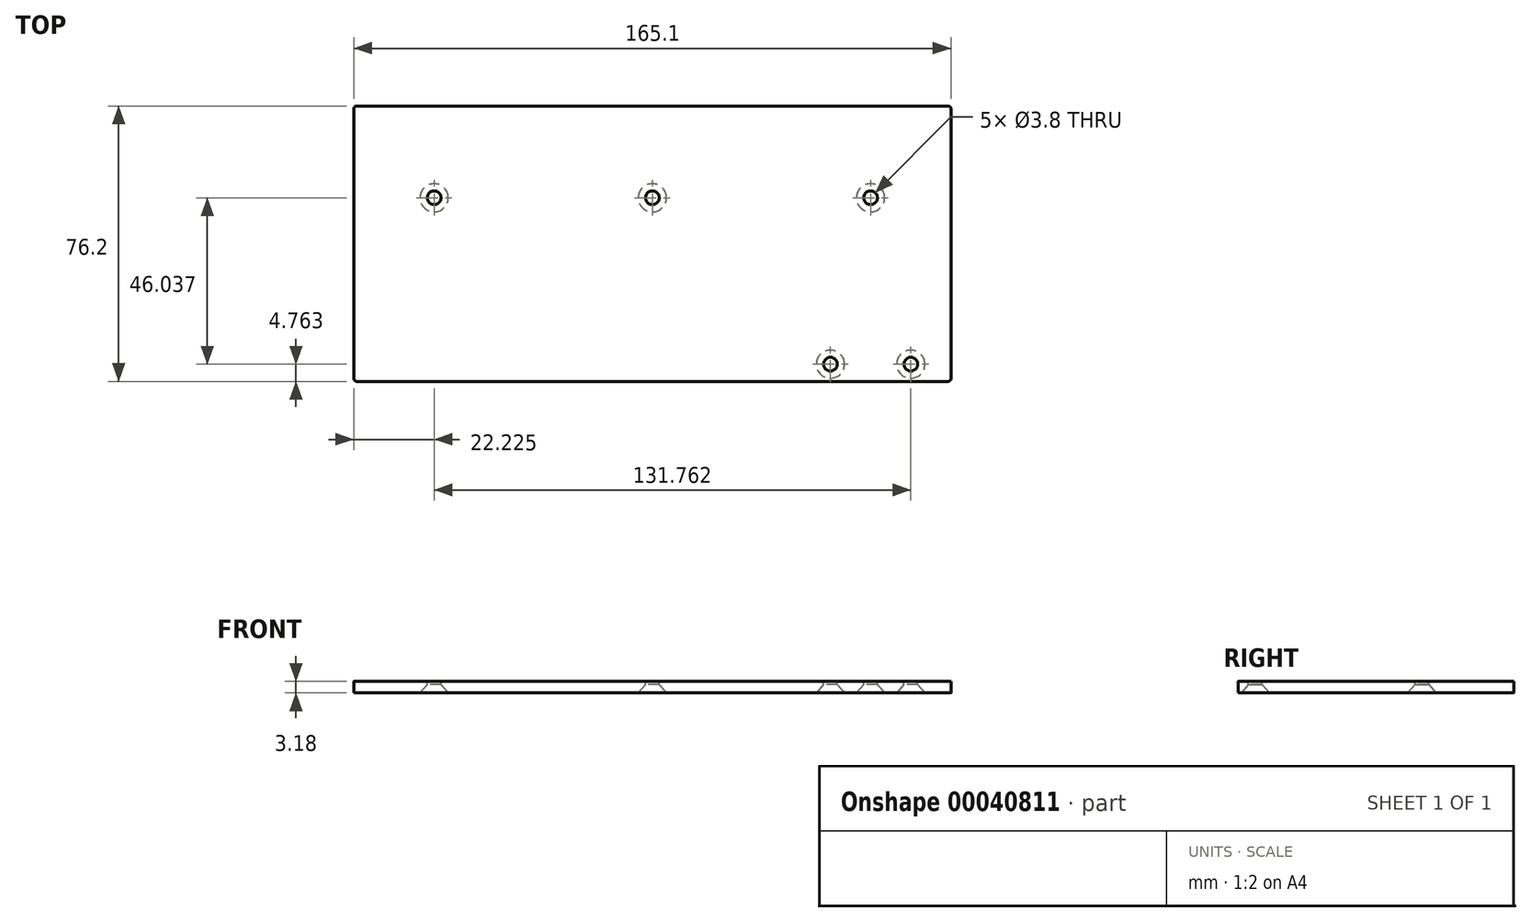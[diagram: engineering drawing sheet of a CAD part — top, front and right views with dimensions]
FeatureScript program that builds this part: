
annotation { "Feature Type Name" : "Feature", "Feature Type Description" : "" }
export const myFeature = defineFeature(function(context is Context, id is Id, definition is map)
    precondition{}
    {
        {
            var Q0;
            Q0=qCreatedBy(makeId("Top.planeOp"),FACE);
            var sketch = newSketch(context, id + "F0", { "sketchPlane" : qUnion([Q0])});
            skLineSegment(sketch, "E0.rect.bottom", {"start": v(-81.76, 38.1) * mm, "end": v(81.76, 38.1) * mm});
            skLineSegment(sketch, "E0.rect.top", {"start": v(-81.76, -38.1) * mm, "end": v(81.76, -38.1) * mm});
            skLineSegment(sketch, "E0.rect.left", {"start": v(-82.55, 37.3) * mm, "end": v(-82.55, -37.3) * mm});
            skLineSegment(sketch, "E0.rect.right", {"start": v(82.55, 37.3) * mm, "end": v(82.55, -37.3) * mm});
            skPoint(sketch, "E0.rect.middle", {"position": v(0, 0) * mm});
            skLineSegment(sketch, "E1", {"start": v(-82.55, 12.7) * mm, "end": v(82.55, 12.7) * mm, "construction": true});
            skLineSegment(sketch, "E2", {"start": v(-82.55, -33.34) * mm, "end": v(82.55, -33.34) * mm, "construction": true});
            skPoint(sketch, "E3.visualSharp", {"position": v(-82.55, 38.1) * mm});
            skArc(sketch, "E3.filletArc", {"start": v(-81.76, 38.1) * mm, "mid": v(-82.32, 37.87) * mm, "end": v(-82.55, 37.3) * mm});
            skPoint(sketch, "E4.visualSharp", {"position": v(-82.55, -38.1) * mm});
            skArc(sketch, "E4.filletArc", {"start": v(-82.55, -37.3) * mm, "mid": v(-82.32, -37.87) * mm, "end": v(-81.76, -38.1) * mm});
            skPoint(sketch, "E5.visualSharp", {"position": v(82.55, -38.1) * mm});
            skArc(sketch, "E5.filletArc", {"start": v(81.76, -38.1) * mm, "mid": v(82.32, -37.87) * mm, "end": v(82.55, -37.3) * mm});
            skPoint(sketch, "E6.visualSharp", {"position": v(82.55, 38.1) * mm});
            skArc(sketch, "E6.filletArc", {"start": v(82.55, 37.3) * mm, "mid": v(82.32, 37.87) * mm, "end": v(81.76, 38.1) * mm});
            skPoint(sketch, "E7", {"position": v(-60.32, 12.7) * mm});
            skPoint(sketch, "E8", {"position": v(0, 12.7) * mm});
            skPoint(sketch, "E9", {"position": v(60.33, 12.7) * mm});
            skPoint(sketch, "E10", {"position": v(71.44, -33.34) * mm});
            skPoint(sketch, "E11", {"position": v(49.21, -33.34) * mm});
            skLineSegment(sketch, "E12", {"start": v(60.33, 12.7) * mm, "end": v(60.33, -33.34) * mm, "construction": true});
            skSolve(sketch);
        }
        {
            var Q0;
            Q0=makeQuery(id+"F0.imprint","IMPRINT",FACE,{"disambiguationData":[TD([[makeQuery(id+"F0.imprint","IMPRINT",EDGE,{"derivedFrom":sQuery(id+"F0.wireOp",EDGE,"E0.rect.bottom")}),-1.0]])]});
            extrude(context, id + "F1", {"entities" : qUnion([Q0]), "depth" : 3.17 * mm});
        }
        {
            var Q0;
            Q0=sQuery(id+"F0.wireOp",VERTEX,"E11");
            var Q1;
            Q1=sQuery(id+"F0.wireOp",VERTEX,"E10");
            var Q2;
            Q2=sQuery(id+"F0.wireOp",VERTEX,"E9");
            var Q3;
            Q3=sQuery(id+"F0.wireOp",VERTEX,"E8");
            var Q4;
            Q4=sQuery(id+"F0.wireOp",VERTEX,"E7");
            var Q5;
            Q5=makeQuery(id+"F1.opExtrude","SWEPT_BODY",BODY,{"disambiguationData":[OSD([sQuery(id+"F0.wireOp",EDGE,"E0.rect.bottom"),sQuery(id+"F0.wireOp",EDGE,"E0.rect.top"),sQuery(id+"F0.wireOp",EDGE,"E0.rect.left"),sQuery(id+"F0.wireOp",EDGE,"E0.rect.right"),sQuery(id+"F0.wireOp",EDGE,"E3.filletArc"),sQuery(id+"F0.wireOp",EDGE,"E4.filletArc"),sQuery(id+"F0.wireOp",EDGE,"E5.filletArc"),sQuery(id+"F0.wireOp",EDGE,"E6.filletArc")])]});
            hole(context, id + "F2", {"style" : HoleStyle.C_SINK, "holeDiameter" : 3.8 * mm, "cSinkDiameter" : 7.8 * mm, "endStyle" : HoleEndStyle.THROUGH, "oppositeDirection" : true, "locations" : qUnion([Q0, Q1, Q2, Q3, Q4]), "scope" : qUnion([Q5]), "cSinkAngle" : 82 * degree, "standardTappedOrClearance" : lookupTablePath({ "standard" : "ANSI", "fit" : "Normal (ASME)", "size" : "#6", "type" : "Clearance" }), "standardBlindInLast" : lookupTablePath({ "fit" : "Free", "standard" : "ANSI", "size" : "#6", "type" : "Clearance" }), "isTappedThrough" : true, "startStyle" : HoleStartStyle.PART});
        }
        {
            var Q0;
            Q0=makeQuery(id+"F0.imprint","IMPRINT",FACE,{"disambiguationData":[TD([[makeQuery(id+"F0.imprint","IMPRINT",EDGE,{"derivedFrom":sQuery(id+"F0.wireOp",EDGE,"E0.rect.bottom")}),-1.0]])]});
            extrude(context, id + "F3", {"entities" : qUnion([Q0]), "depth" : 3.17 * mm});
        }
    });
